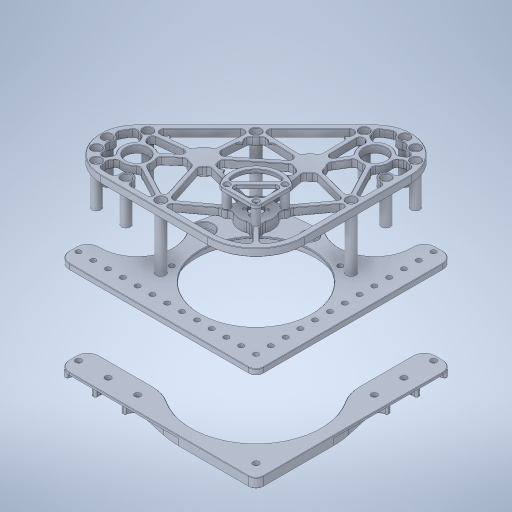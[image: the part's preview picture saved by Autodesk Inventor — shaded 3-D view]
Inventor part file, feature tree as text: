
AUTODESK INVENTOR PART (.ipt)
format: ipt  version: 2023.3 (Build 273359000, 359)  size: 1,730,560 bytes
history: native  units: in
note: dims shown in document units (in); Inventor stores cm internally (conversion verified against a paired STEP export)
features: other x14, chamfer x4, direct_edit x1, move_body x1
ambient origin geometry x8: Origin, YZ Plane, XZ Plane, XY Plane, X Axis, Y Axis, Z Axis, Center Point
bodies: Solid1 (feature_tree), Solid2 (feature_tree), Solid3 (feature_tree), Solid4 (feature_tree), Solid5 (feature_tree), Solid6 (feature_tree), Solid7 (feature_tree), Solid8 (feature_tree), Solid9 (feature_tree), Solid10 (feature_tree), Solid11 (feature_tree), Solid13 (feature_tree), Solid14 (feature_tree), Solid15 (feature_tree), Solid16 (feature_tree), Solid17 (feature_tree), Solid18 (feature_tree), Solid19 (feature_tree)
feature tree (20):
  direct_edit  "Direct Edit1"
  other  "Boss-Extrude4[1]"
  other  "Boss-Extrude4[2]"
  other  "Boss-Extrude4[3]"
  other  "Boss-Extrude6[1]"
  other  "Boss-Extrude6[2]"
  other  "Boss-Extrude6[3]"
  other  "Boss-Extrude6[4]"
  other  "Boss-Extrude6[5]"
  other  "Boss-Extrude6[6]"
  other  "Boss-Extrude6[7]"
  other  "Boss-Extrude6[8]"
  other  "Boss-Extrude17[1]"
  other  "Boss-Extrude17[2]"
  other  "Boss-Extrude17[3]"
  chamfer  "Chamfer4"  [1 undecoded]
  chamfer  "Chamfer1"  [1 undecoded]
  chamfer  "Chamfer3"  [1 undecoded]
  chamfer  "Chamfer2"  [1 undecoded]
  move_body  "Move1"
note: 4 required parameter values undecoded (feature->parameter linkage not recoverable at this tier; creation-order binding heuristic only, values carry confidence <= 0.55)
